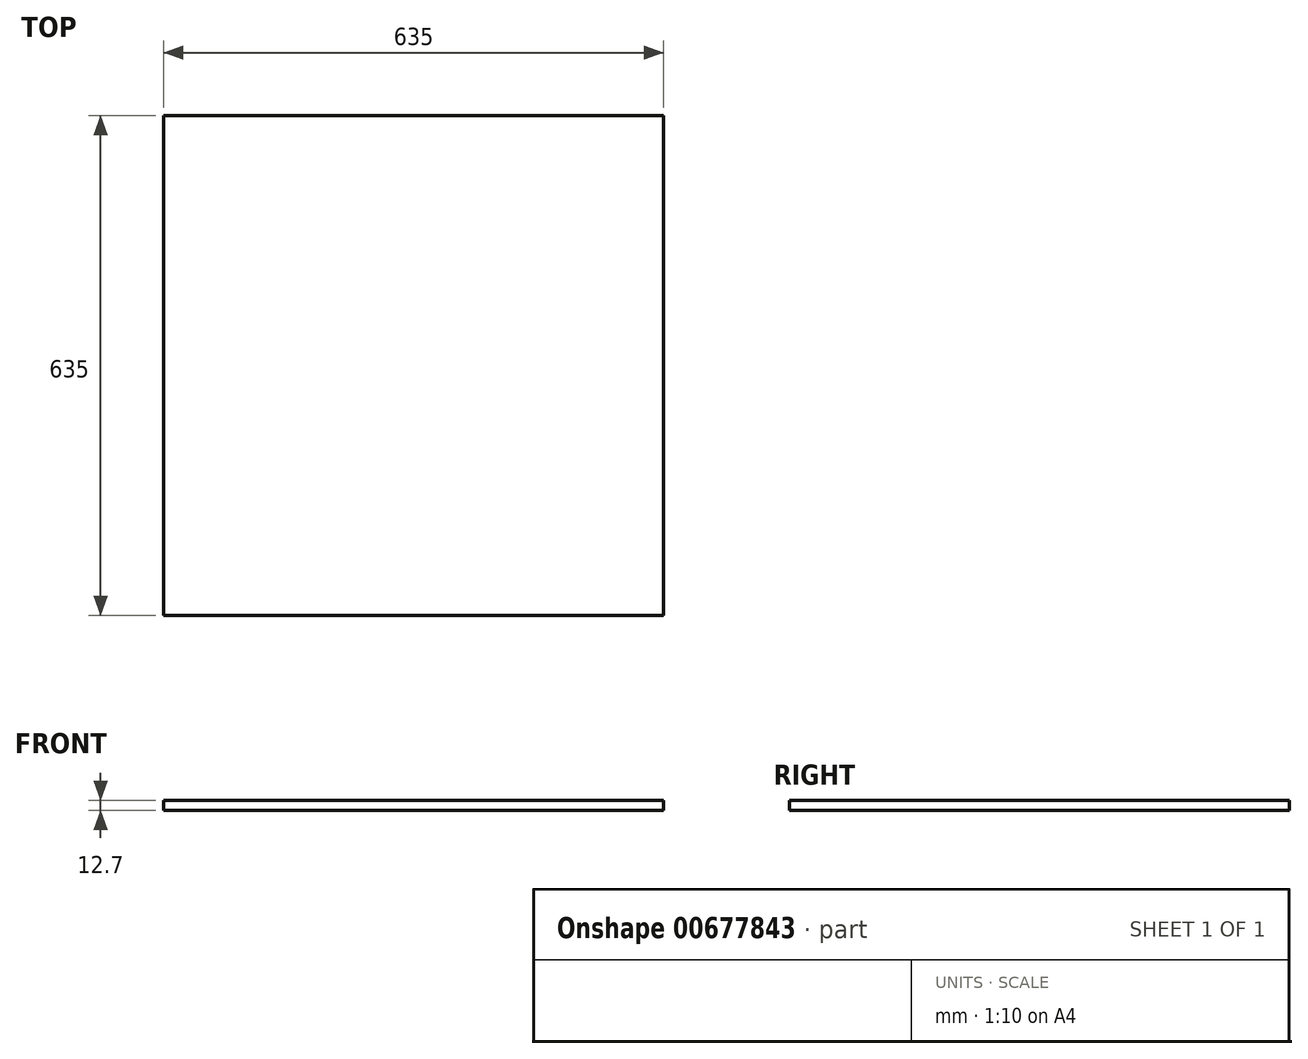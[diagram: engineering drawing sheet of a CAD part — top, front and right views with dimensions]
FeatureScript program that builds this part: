
annotation { "Feature Type Name" : "Feature", "Feature Type Description" : "" }
export const myFeature = defineFeature(function(context is Context, id is Id, definition is map)
    precondition{}
    {
        {
            var Q0;
            Q0=qCreatedBy(makeId("Top.planeOp"),FACE);
            var sketch = newSketch(context, id + "F0", { "sketchPlane" : qUnion([Q0])});
            skLineSegment(sketch, "E0.bottom", {"start": v(0, 0) * mm, "end": v(635, 0) * mm});
            skLineSegment(sketch, "E0.top", {"start": v(0, -635) * mm, "end": v(635, -635) * mm});
            skLineSegment(sketch, "E0.left", {"start": v(0, 0) * mm, "end": v(0, -635) * mm});
            skLineSegment(sketch, "E0.right", {"start": v(635, 0) * mm, "end": v(635, -635) * mm});
            skSolve(sketch);
        }
        {
            var Q0;
            Q0 = qSketchRegion(id + "F0", true);
            extrude(context, id + "F1", {"entities" : qUnion([Q0]), "depth" : 12.7 * mm, "offsetDistance" : 25.4 * mm});
        }
    });
